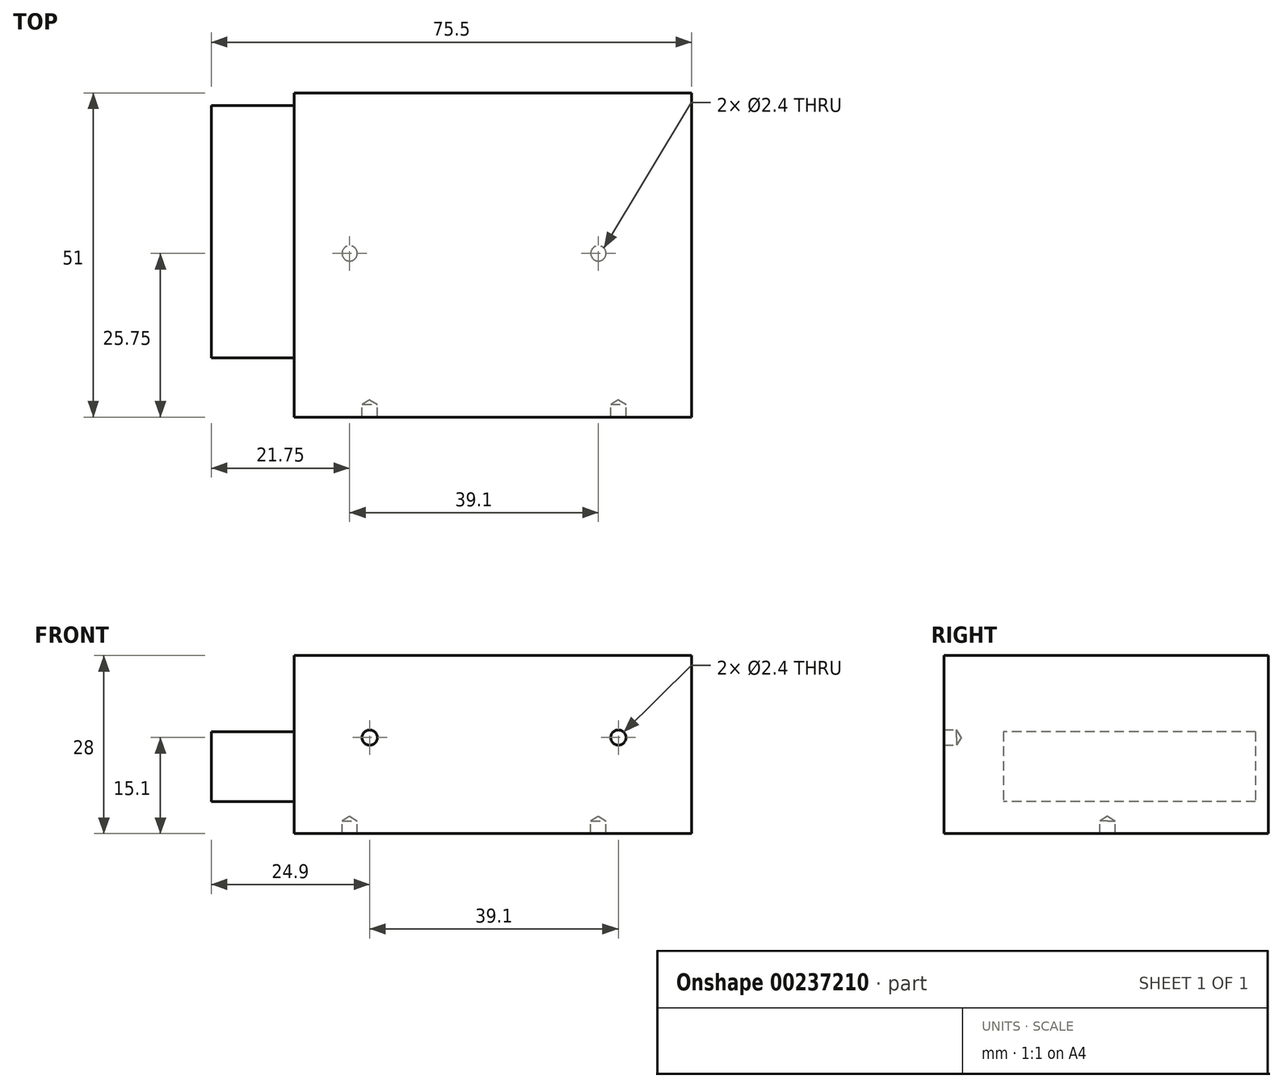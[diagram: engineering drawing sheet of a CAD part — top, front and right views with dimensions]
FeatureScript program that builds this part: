
annotation { "Feature Type Name" : "Feature", "Feature Type Description" : "" }
export const myFeature = defineFeature(function(context is Context, id is Id, definition is map)
    precondition{}
    {
        {
            var Q0;
            Q0=qCreatedBy(makeId("Top.planeOp"),FACE);
            var sketch = newSketch(context, id + "F0", { "sketchPlane" : qUnion([Q0])});
            skLineSegment(sketch, "E0.bottom", {"start": v(-31.25, 25.5) * mm, "end": v(31.25, 25.5) * mm});
            skLineSegment(sketch, "E0.top", {"start": v(-31.25, -25.5) * mm, "end": v(31.25, -25.5) * mm});
            skLineSegment(sketch, "E0.left", {"start": v(-31.25, 25.5) * mm, "end": v(-31.25, -25.5) * mm});
            skLineSegment(sketch, "E0.right", {"start": v(31.25, 25.5) * mm, "end": v(31.25, -25.5) * mm});
            skPoint(sketch, "E1", {"position": v(0, 25.5) * mm});
            skPoint(sketch, "E2", {"position": v(-31.25, 0) * mm});
            skLineSegment(sketch, "E3.bottom", {"start": v(-31.25, 23.5) * mm, "end": v(-44.25, 23.5) * mm});
            skLineSegment(sketch, "E3.top", {"start": v(-31.25, -16.16) * mm, "end": v(-44.25, -16.16) * mm});
            skLineSegment(sketch, "E3.left", {"start": v(-31.25, 23.5) * mm, "end": v(-31.25, -16.16) * mm});
            skLineSegment(sketch, "E3.right", {"start": v(-44.25, 23.5) * mm, "end": v(-44.25, -16.16) * mm});
            skSolve(sketch);
        }
        {
            var Q0;
            {var subQ3=sQuery(id+"F0.wireOp",EDGE,"E0.bottom");Q0=makeQuery(id+"F0.imprint","IMPRINT",FACE,{"disambiguationData":[TD([[makeQuery(id+"F0.imprint","IMPRINT",EDGE,{"derivedFrom":subQ3}),-1.0]])]});}
            var Q1;
            Q1=makeQuery(id+"F0.imprint","IMPRINT",FACE,{"disambiguationData":[TD([[makeQuery(id+"F0.imprint","IMPRINT",EDGE,{"derivedFrom":sQuery(id+"F0.wireOp",EDGE,"E3.bottom")}),1.0]])]});
            extrude(context, id + "F1", {"entities" : qUnion([Q0, Q1]), "depth" : 28 * mm});
        }
        {
            var Q0;
            Q0=makeQuery(id+"F1.opExtrude","CAP_FACE",FACE,{"disambiguationData":[OSD([sQuery(id+"F0.wireOp",EDGE,"E0.bottom"),sQuery(id+"F0.wireOp",EDGE,"E0.top"),sQuery(id+"F0.wireOp",EDGE,"E0.left"),sQuery(id+"F0.wireOp",EDGE,"E0.right"),sQuery(id+"F0.wireOp",EDGE,"E3.bottom"),sQuery(id+"F0.wireOp",EDGE,"E3.top"),sQuery(id+"F0.wireOp",EDGE,"E3.right")])],"isStart":false});
            var sketch = newSketch(context, id + "F2", { "sketchPlane" : qUnion([Q0])});
            skLineSegment(sketch, "E4.bottom", {"start": v(-44.25, 23.5) * mm, "end": v(-31.25, 23.5) * mm});
            skLineSegment(sketch, "E4.top", {"start": v(-44.25, -16.16) * mm, "end": v(-31.25, -16.16) * mm});
            skLineSegment(sketch, "E4.left", {"start": v(-44.25, 23.5) * mm, "end": v(-44.25, -16.16) * mm});
            skLineSegment(sketch, "E4.right", {"start": v(-31.25, 23.5) * mm, "end": v(-31.25, -16.16) * mm});
            skSolve(sketch);
        }
        {
            var Q0;
            Q0=makeQuery(id+"F2.imprint","IMPRINT",FACE,{"disambiguationData":[TD([[makeQuery(id+"F2.imprint","IMPRINT",EDGE,{"derivedFrom":sQuery(id+"F2.wireOp",EDGE,"E4.bottom")}),1.0]])]});
            extrude(context, id + "F3", {"entities" : qUnion([Q0]), "operationType" : NewBodyOperationType.REMOVE, "oppositeDirection" : true, "depth" : 12 * mm});
        }
        {
            var Q0;
            Q0=makeQuery(id+"F1.opExtrude","CAP_FACE",FACE,{"disambiguationData":[OSD([sQuery(id+"F0.wireOp",EDGE,"E0.bottom"),sQuery(id+"F0.wireOp",EDGE,"E0.top"),sQuery(id+"F0.wireOp",EDGE,"E0.left"),sQuery(id+"F0.wireOp",EDGE,"E0.right"),sQuery(id+"F0.wireOp",EDGE,"E3.bottom"),sQuery(id+"F0.wireOp",EDGE,"E3.top"),sQuery(id+"F0.wireOp",EDGE,"E3.right")])],"isStart":true});
            var sketch = newSketch(context, id + "F4", { "sketchPlane" : qUnion([Q0])});
            skLineSegment(sketch, "E5.bottom", {"start": v(-44.25, 16.16) * mm, "end": v(-31.25, 16.16) * mm});
            skLineSegment(sketch, "E5.top", {"start": v(-44.25, -23.5) * mm, "end": v(-31.25, -23.5) * mm});
            skLineSegment(sketch, "E5.left", {"start": v(-44.25, 16.16) * mm, "end": v(-44.25, -23.5) * mm});
            skLineSegment(sketch, "E5.right", {"start": v(-31.25, 16.16) * mm, "end": v(-31.25, -23.5) * mm});
            skSolve(sketch);
        }
        {
            var Q0;
            Q0=makeQuery(id+"F4.imprint","IMPRINT",FACE,{"disambiguationData":[TD([[makeQuery(id+"F4.imprint","IMPRINT",EDGE,{"derivedFrom":sQuery(id+"F4.wireOp",EDGE,"E5.bottom")}),1.0]])]});
            extrude(context, id + "F5", {"entities" : qUnion([Q0]), "operationType" : NewBodyOperationType.REMOVE, "oppositeDirection" : true, "depth" : 5 * mm});
        }
        {
            var Q0;
            Q0=makeQuery(id+"F1.opExtrude","SWEPT_FACE",FACE,{"disambiguationData":[OSD([sQuery(id+"F0.wireOp",EDGE,"E0.top")])]});
            var sketch = newSketch(context, id + "F6", { "sketchPlane" : qUnion([Q0])});
            skPoint(sketch, "E6", {"position": v(19.75, 15.1) * mm});
            skPoint(sketch, "E7", {"position": v(-19.35, 15.1) * mm});
            skSolve(sketch);
        }
        {
            var Q0;
            Q0=makeQuery(id+"F1.opExtrude","CAP_FACE",FACE,{"disambiguationData":[OSD([sQuery(id+"F0.wireOp",EDGE,"E0.bottom"),sQuery(id+"F0.wireOp",EDGE,"E0.top"),sQuery(id+"F0.wireOp",EDGE,"E0.left"),sQuery(id+"F0.wireOp",EDGE,"E0.right"),sQuery(id+"F0.wireOp",EDGE,"E3.bottom"),sQuery(id+"F0.wireOp",EDGE,"E3.top"),sQuery(id+"F0.wireOp",EDGE,"E3.right")])],"isStart":true});
            var sketch = newSketch(context, id + "F7", { "sketchPlane" : qUnion([Q0])});
            skPoint(sketch, "E8", {"position": v(-22.5, -0.25) * mm});
            skPoint(sketch, "E9", {"position": v(16.6, -0.25) * mm});
            skSolve(sketch);
        }
        {
            var Q0;
            Q0=sQuery(id+"F7.wireOp",VERTEX,"E8");
            var Q1;
            Q1=sQuery(id+"F7.wireOp",VERTEX,"E9");
            var Q2;
            Q2=sQuery(id+"F6.wireOp",VERTEX,"E7");
            var Q3;
            Q3=sQuery(id+"F6.wireOp",VERTEX,"E6");
            var Q4;
            Q4=makeQuery(id+"F1.opExtrude","SWEPT_BODY",BODY,{"disambiguationData":[OSD([sQuery(id+"F0.wireOp",EDGE,"E0.bottom"),sQuery(id+"F0.wireOp",EDGE,"E0.top"),sQuery(id+"F0.wireOp",EDGE,"E0.left"),sQuery(id+"F0.wireOp",EDGE,"E0.right"),sQuery(id+"F0.wireOp",EDGE,"E3.bottom"),sQuery(id+"F0.wireOp",EDGE,"E3.top"),sQuery(id+"F0.wireOp",EDGE,"E3.right")])]});
            hole(context, id + "F8", {"style" : HoleStyle.SIMPLE, "endStyle" : HoleEndStyle.BLIND, "standardTappedOrClearance" : lookupTablePath({ "standard" : "ISO", "engagement" : "75%", "pitch" : "0.6 mm", "size" : "M3", "type" : "Tapped" }), "standardBlindInLast" : lookupTablePath({ "standard" : "ISO", "engagement" : "75%", "pitch" : "0.6 mm", "size" : "M3", "type" : "Tapped" }), "holeDiameter" : 2.4 * mm, "holeDepth" : 2 * mm, "startFromSketch" : true, "locations" : qUnion([Q0, Q1, Q2, Q3]), "scope" : qUnion([Q4])});
        }
    });
